# Revit family: Trap_Primer_Automatic Sani-Gard-Zurn-Z1022-XL
name_source: partatom
category: Plumbing Fixtures
units: mm (PartAtom-declared; Revit-internal decimal feet)

## family parameters
Always vertical = Yes
Cut with Voids When Loaded = No
Maintain Annotation Orientation = No
OmniClass Number = 23.45.55.21
OmniClass Title = Drains (Wastes)
Part Type = Normal
Room Calculation Point = No
Round Connector Dimension = Use Radius
Shared = No
Work Plane-Based = No

## types (5) — shared parameters
Assembly Code = D2090800
CW Connection = No
Default Elevation = 20 "
Description = SANI-GARD AUTOMATIC TRAP PRIMER
HW Connection = No
Main Material = Bronze - Zurn - Polished
Manufacturer = Zurn Water, LLC
Manufacurer Brand = Zurn
Model = Z1022-XL
Modified Date = 02/20/2026
Product Documentation Link = https://files.zurn.com
Product Installation Sheet URL = https://files.zurn.com
Product Page URL = https://www.zurn.com
Product data url = https://www.bimobject.com
URL = www.zurn.com
Vent Connection = No
WFU = 1
Waste Connection = Yes
zero-valued in all types: CWFU, HWFU

## per-type parameters (varying)
| type | Approx Weight | Connector Radius | Length_L | Pipe Size_A Inside Diameter | Pipe Size_A Nominal Diameter | Pipe Size_A Outer Diameter |
| Z1022-XL 1/2 Inch Solder Female | 1.00 lb | 0.25 " | 3.219 " | 0.622 " | 0.5 " | 0.84 " |
| Z1022-XL 3/4 Inch IP Male Union | 1.50 lb | 0.375 " | 6.844 " | 0.824 " | 0.75 " | 1.05 " |
| Z1022-XL 1/2 Inch IP Female | 1.00 lb | 0.25 " | 3.219 " | 0.622 " | 0.5 " | 0.84 " |
| Z1022-XL 1/2 Inch IP Female Union | 1.50 lb | 0.25 " | 5.344 " | 0.622 " | 0.5 " | 0.84 " |
| Z1022-XL 1/2 Inch Solder Female Union | 1.50 lb | 0.25 " | 5.656 " | 0.622 " | 0.5 " | 0.84 " |

## geometry (parser evidence)
native form markers: Blend x4, Sweep x2
no freeform markers — native parametric forms only
